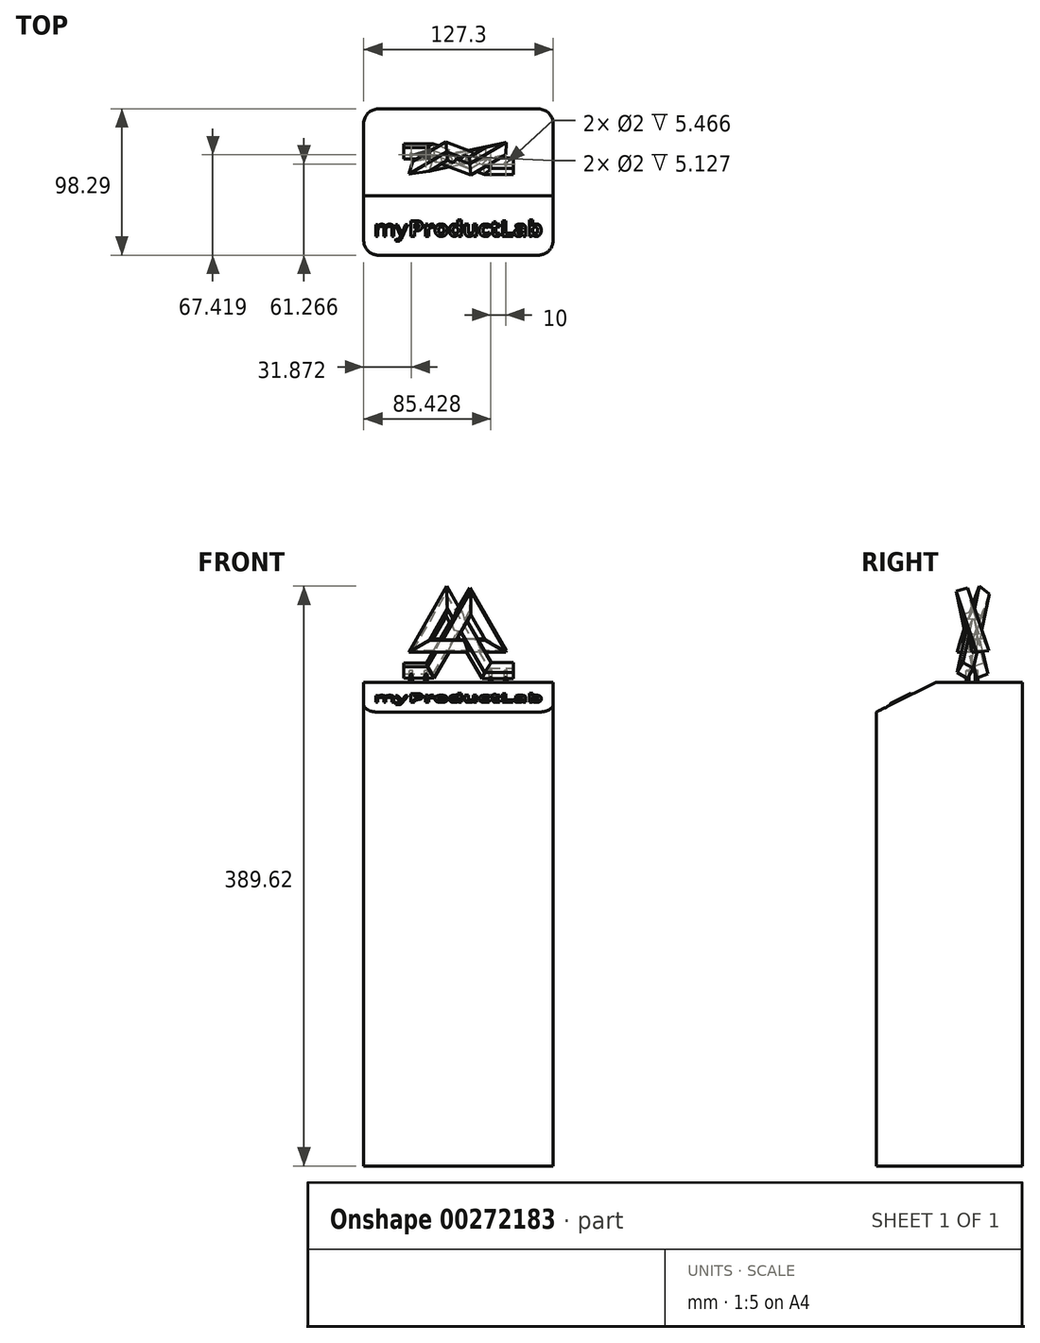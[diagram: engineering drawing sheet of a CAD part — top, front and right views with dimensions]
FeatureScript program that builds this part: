
annotation { "Feature Type Name" : "Feature", "Feature Type Description" : "" }
export const myFeature = defineFeature(function(context is Context, id is Id, definition is map)
    precondition{}
    {
        {
            var Q0;
            Q0=qCreatedBy(makeId("Front.planeOp"),FACE);
            var sketch = newSketch(context, id + "F0", { "sketchPlane" : qUnion([Q0])});
            skLineSegment(sketch, "E0", {"start": v(-36.78, 0) * mm, "end": v(-18.91, 0) * mm});
            skLineSegment(sketch, "E1", {"start": v(-18.91, 0) * mm, "end": v(7.93, 46.5) * mm});
            skLineSegment(sketch, "E2", {"start": v(7.93, 46.5) * mm, "end": v(25.1, 16.76) * mm});
            skLineSegment(sketch, "E3", {"start": v(25.1, 16.76) * mm, "end": v(-25.1, 16.76) * mm});
            skLineSegment(sketch, "E4", {"start": v(-25.1, 16.76) * mm, "end": v(-7.93, 46.5) * mm});
            skLineSegment(sketch, "E5", {"start": v(-7.93, 46.5) * mm, "end": v(18.91, 0) * mm});
            skLineSegment(sketch, "E6", {"start": v(18.91, 0) * mm, "end": v(36.78, 0) * mm});
            skPoint(sketch, "E7", {"position": v(0, 32.76) * mm});
            skPoint(sketch, "E8", {"position": v(0, 16.76) * mm});
            skSolve(sketch);
        }
        {
            var Q0;
            Q0=qCreatedBy(makeId("Front.planeOp"),FACE);
            cPlane(context, id + "F1", {"entities" : qUnion([Q0]), "cplaneType" : CPlaneType.OFFSET, "offset" : 10 * mm, "oppositeDirection" : true, "width" : 150 * mm, "height" : 150 * mm});
        }
        {
            var Q0;
            Q0=qCreatedBy(id+"F1.planeOp",FACE);
            var sketch = newSketch(context, id + "F2", { "sketchPlane" : qUnion([Q0])});
            skPoint(sketch, "E9", {"position": v(-36.78, 0) * mm});
            skPoint(sketch, "E10", {"position": v(-18.91, 0) * mm});
            skPoint(sketch, "E11", {"position": v(25.1, 16.76) * mm});
            skPoint(sketch, "E12", {"position": v(-7.93, 46.5) * mm});
            skSolve(sketch);
        }
        {
            var Q0;
            Q0=qCreatedBy(makeId("Front.planeOp"),FACE);
            var sketch = newSketch(context, id + "F3", { "sketchPlane" : qUnion([Q0])});
            skPoint(sketch, "E13", {"position": v(-25.1, 16.76) * mm});
            skPoint(sketch, "E14", {"position": v(7.93, 46.5) * mm});
            skPoint(sketch, "E15", {"position": v(18.91, 0) * mm});
            skPoint(sketch, "E16", {"position": v(36.78, 0) * mm});
            skSolve(sketch);
        }
        {
            var Q0;
            Q0=sQuery(id+"F2.wireOp",VERTEX,"E12");
            var Q1;
            Q1=sQuery(id+"F2.wireOp",VERTEX,"E10");
            var Q2;
            Q2=sQuery(id+"F3.wireOp",VERTEX,"E14");
            cPlane(context, id + "F4", {"entities" : qUnion([Q0, Q1, Q2]), "cplaneType" : CPlaneType.THREE_POINT, "offset" : 25 * mm, "width" : 150 * mm, "height" : 150 * mm});
        }
        {
            var Q0;
            Q0=sQuery(id+"F3.wireOp",VERTEX,"E14");
            var Q1;
            Q1=sQuery(id+"F2.wireOp",VERTEX,"E11");
            var Q2;
            Q2=sQuery(id+"F3.wireOp",VERTEX,"E13");
            cPlane(context, id + "F5", {"entities" : qUnion([Q0, Q1, Q2]), "cplaneType" : CPlaneType.THREE_POINT, "offset" : 25 * mm, "width" : 150 * mm, "height" : 150 * mm});
        }
        {
            var Q0;
            Q0=qCreatedBy(id+"F1.planeOp",FACE);
            var sketch = newSketch(context, id + "F6", { "sketchPlane" : qUnion([Q0])});
            skLineSegment(sketch, "E17", {"start": v(-36.78, 0) * mm, "end": v(-18.91, 0) * mm});
            skSolve(sketch);
        }
        {
            var Q0;
            Q0=qCreatedBy(id+"F4.planeOp",FACE);
            var sketch = newSketch(context, id + "F7", { "sketchPlane" : qUnion([Q0])});
            skLineSegment(sketch, "E18", {"start": v(21.28, 1.47) * mm, "end": v(-10.35, 46) * mm});
            skSolve(sketch);
        }
        {
            var Q0;
            Q0=qCreatedBy(id+"F5.planeOp",FACE);
            var sketch = newSketch(context, id + "F8", { "sketchPlane" : qUnion([Q0])});
            skLineSegment(sketch, "E19", {"start": v(9.7, 45.4) * mm, "end": v(27.2, 14.2) * mm});
            skSolve(sketch);
        }
        {
            var Q0;
            Q0=qCreatedBy(id+"F5.planeOp",FACE);
            var sketch = newSketch(context, id + "F9", { "sketchPlane" : qUnion([Q0])});
            skLineSegment(sketch, "E20", {"start": v(1.62, 15.29) * mm, "end": v(-23.95, 16.37) * mm});
            skLineSegment(sketch, "E21", {"start": v(27.2, 14.2) * mm, "end": v(1.62, 15.29) * mm});
            skSolve(sketch);
        }
        {
            var Q0;
            Q0=sQuery(id+"F2.wireOp",VERTEX,"E12");
            var Q1;
            Q1=sQuery(id+"F3.wireOp",VERTEX,"E13");
            var Q2;
            Q2=sQuery(id+"F2.wireOp",VERTEX,"E10");
            cPlane(context, id + "F10", {"entities" : qUnion([Q0, Q1, Q2]), "cplaneType" : CPlaneType.THREE_POINT, "offset" : 25 * mm, "width" : 150 * mm, "height" : 150 * mm});
        }
        {
            var Q0;
            Q0=qCreatedBy(id+"F10.planeOp",FACE);
            var sketch = newSketch(context, id + "F11", { "sketchPlane" : qUnion([Q0])});
            skLineSegment(sketch, "E22", {"start": v(-8.31, 43.03) * mm, "end": v(15.48, 16.33) * mm});
            skSolve(sketch);
        }
        {
            var Q0;
            Q0=sQuery(id+"F2.wireOp",VERTEX,"E12");
            var Q1;
            Q1=sQuery(id+"F3.wireOp",VERTEX,"E15");
            var Q2;
            Q2=sQuery(id+"F3.wireOp",VERTEX,"E16");
            cPlane(context, id + "F12", {"entities" : qUnion([Q0, Q1, Q2]), "cplaneType" : CPlaneType.THREE_POINT, "offset" : 25 * mm, "width" : 150 * mm, "height" : 150 * mm});
        }
        {
            var Q0;
            Q0=qCreatedBy(id+"F12.planeOp",FACE);
            var sketch = newSketch(context, id + "F13", { "sketchPlane" : qUnion([Q0])});
            skLineSegment(sketch, "E23", {"start": v(7.93, 47.56) * mm, "end": v(-18.91, 0) * mm});
            skLineSegment(sketch, "E24", {"start": v(-18.91, 0) * mm, "end": v(-36.78, 0) * mm});
            skSolve(sketch);
        }
        {
            var Q0;
            Q0=sQuery(id+"F6.wireOp",EDGE,"E17");
            var Q1;
            Q1=sQuery(id+"F6.wireOp",VERTEX,"E17.start");
            cPlane(context, id + "F14", {"entities" : qUnion([Q0, Q1]), "cplaneType" : CPlaneType.LINE_POINT, "offset" : 25 * mm, "width" : 150 * mm, "height" : 150 * mm});
        }
        {
            var Q0;
            Q0=qCreatedBy(id+"F14.planeOp",FACE);
            var sketch = newSketch(context, id + "F15", { "sketchPlane" : qUnion([Q0])});
            skLineSegment(sketch, "E25.bottom", {"start": v(6, 4) * mm, "end": v(14, 4) * mm, "construction": true});
            skLineSegment(sketch, "E25.top", {"start": v(6, -4) * mm, "end": v(14, -4) * mm, "construction": true});
            skLineSegment(sketch, "E25.left", {"start": v(6, 4) * mm, "end": v(6, -4) * mm, "construction": true});
            skLineSegment(sketch, "E25.right", {"start": v(14, 4) * mm, "end": v(14, -4) * mm, "construction": true});
            skPoint(sketch, "E25.middle", {"position": v(10, 0) * mm});
            skLineSegment(sketch, "E26", {"start": v(7.6, -5.13) * mm, "end": v(15.13, -2.4) * mm});
            skLineSegment(sketch, "E27", {"start": v(15.13, -2.4) * mm, "end": v(12.4, 5.13) * mm});
            skLineSegment(sketch, "E28", {"start": v(12.4, 5.13) * mm, "end": v(4.87, 2.4) * mm});
            skLineSegment(sketch, "E29", {"start": v(4.87, 2.4) * mm, "end": v(7.6, -5.13) * mm});
            skLineSegment(sketch, "E30", {"start": v(7.6, -5.13) * mm, "end": v(12.4, 5.13) * mm, "construction": true});
            skLineSegment(sketch, "E31", {"start": v(15.13, -2.4) * mm, "end": v(4.87, 2.4) * mm, "construction": true});
            skSolve(sketch);
        }
        {
            var Q0;
            Q0=makeQuery(id+"F15.imprint","IMPRINT",FACE,{"disambiguationData":[TD([[makeQuery(id+"F15.imprint","IMPRINT",EDGE,{"derivedFrom":sQuery(id+"F15.wireOp",EDGE,"E26")}),1.0]])]});
            var Q1;
            Q1=sQuery(id+"F6.wireOp",EDGE,"E17");
            var Q2;
            Q2=sQuery(id+"F7.wireOp",EDGE,"E18");
            var Q3;
            Q3=sQuery(id+"F8.wireOp",EDGE,"E19");
            var Q4;
            Q4=sQuery(id+"F9.wireOp",EDGE,"E21");
            sweep(context, id + "F16", {"profiles" : qUnion([Q0]), "path" : qUnion([Q1, Q2, Q3, Q4])});
        }
        {
            var Q0;
            Q0=sQuery(id+"F13.wireOp",EDGE,"E24");
            var Q1;
            Q1=sQuery(id+"F13.wireOp",VERTEX,"E24.end");
            cPlane(context, id + "F17", {"entities" : qUnion([Q0, Q1]), "cplaneType" : CPlaneType.LINE_POINT, "offset" : 25 * mm, "width" : 150 * mm, "height" : 150 * mm});
        }
        {
            var Q0;
            Q0=qCreatedBy(id+"F17.planeOp",FACE);
            var sketch = newSketch(context, id + "F18", { "sketchPlane" : qUnion([Q0])});
            skLineSegment(sketch, "E32.bottom", {"start": v(4, -4) * mm, "end": v(-4, -4) * mm});
            skLineSegment(sketch, "E32.top", {"start": v(4, 4) * mm, "end": v(-4, 4) * mm});
            skLineSegment(sketch, "E32.left", {"start": v(4, -4) * mm, "end": v(4, 4) * mm});
            skLineSegment(sketch, "E32.right", {"start": v(-4, -4) * mm, "end": v(-4, 4) * mm});
            skPoint(sketch, "E32.middle", {"position": v(0, 0) * mm});
            skSolve(sketch);
        }
        {
            var Q0;
            Q0=makeQuery(id+"F16.opSweep","CAP_FACE",FACE,{"disambiguationData":[OSD([sQuery(id+"F9.wireOp",VERTEX,"E21.end"),sQuery(id+"F15.wireOp",EDGE,"E26"),sQuery(id+"F15.wireOp",EDGE,"E27"),sQuery(id+"F15.wireOp",EDGE,"E28"),sQuery(id+"F15.wireOp",EDGE,"E29")])],"isStart":false});
            var sketch = newSketch(context, id + "F19", { "sketchPlane" : qUnion([Q0])});
            skLineSegment(sketch, "E33.0", {"start": v(-9.24, 13.13) * mm, "end": v(-1.27, 12.43) * mm});
            skLineSegment(sketch, "E34", {"start": v(-1.27, 12.43) * mm, "end": v(-0.57, 20.4) * mm});
            skLineSegment(sketch, "E35", {"start": v(-0.57, 20.4) * mm, "end": v(-8.54, 21.1) * mm});
            skLineSegment(sketch, "E36", {"start": v(-8.54, 21.1) * mm, "end": v(-9.24, 13.13) * mm});
            skSolve(sketch);
        }
        {
            var Q0;
            Q0 = qSketchRegion(id + "F19", true);
            var Q1;
            Q1=sQuery(id+"F9.wireOp",EDGE,"E20");
            var Q2;
            Q2=sQuery(id+"F11.wireOp",EDGE,"E22");
            var Q3;
            Q3=sQuery(id+"F13.wireOp",EDGE,"E23");
            var Q4;
            Q4=sQuery(id+"F13.wireOp",EDGE,"E24");
            sweep(context, id + "F20", {"operationType" : NewBodyOperationType.ADD, "profiles" : qUnion([Q0]), "path" : qUnion([Q1, Q2, Q3, Q4])});
        }
        {
            var Q0;
            Q0=qCreatedBy(makeId("Top.planeOp"),FACE);
            var sketch = newSketch(context, id + "F21", { "sketchPlane" : qUnion([Q0])});
            skCircle(sketch, "E37", {"center": v(-31.78, 7.6) * mm, "radius": 1 * mm});
            skCircle(sketch, "E38", {"center": v(-21.78, 7.6) * mm, "radius": 1 * mm});
            skCircle(sketch, "E39", {"center": v(21.78, 1.46) * mm, "radius": 1 * mm});
            skCircle(sketch, "E40", {"center": v(31.78, 1.46) * mm, "radius": 1 * mm});
            skSolve(sketch);
        }
        {
            var Q0;
            Q0 = qSketchRegion(id + "F21", true);
            extrude(context, id + "F22", {"entities" : qUnion([Q0]), "operationType" : NewBodyOperationType.REMOVE, "oppositeDirection" : true, "depth" : 25 * mm});
        }
        {
            var Q0;
            Q0 = qSketchRegion(id + "F21", true);
            extrude(context, id + "F23", {"entities" : qUnion([Q0]), "oppositeDirection" : true, "depth" : 10 * mm});
        }
        {
            var Q0;
            Q0=qCreatedBy(makeId("Top.planeOp"),FACE);
            cPlane(context, id + "F24", {"entities" : qUnion([Q0]), "cplaneType" : CPlaneType.OFFSET, "offset" : 8 * mm, "oppositeDirection" : true, "width" : 150 * mm, "height" : 150 * mm});
        }
        {
            var Q0;
            Q0=qCreatedBy(id+"F24.planeOp",FACE);
            var sketch = newSketch(context, id + "F25", { "sketchPlane" : qUnion([Q0])});
            skLineSegment(sketch, "E41.bottom", {"start": v(-63.65, 38.48) * mm, "end": v(63.65, 38.48) * mm});
            skLineSegment(sketch, "E41.top", {"start": v(-63.65, -59.81) * mm, "end": v(63.65, -59.81) * mm});
            skLineSegment(sketch, "E41.left", {"start": v(-63.65, 38.48) * mm, "end": v(-63.65, -59.81) * mm});
            skLineSegment(sketch, "E41.right", {"start": v(63.65, 38.48) * mm, "end": v(63.65, -59.81) * mm});
            skPoint(sketch, "E41.middle", {"position": v(0, -10.67) * mm});
            skSolve(sketch);
        }
        {
            var Q0;
            Q0 = qSketchRegion(id + "F25", true);
            extrude(context, id + "F26", {"entities" : qUnion([Q0]), "oppositeDirection" : true, "depth" : 25 * mm});
        }
        {
            var Q0;
            Q0=makeQuery(id+"F26.opExtrude","CAP_EDGE",EDGE,{"disambiguationData":[OSD([sQuery(id+"F25.wireOp",EDGE,"E41.top")])],"isStart":true});
            chamfer(context, id + "F27", {"entities" : qUnion([Q0]), "chamferType" : ChamferType.TWO_OFFSETS, "width1" : 40 * mm, "oppositeDirection" : false, "width2" : 20 * mm, "tangentPropagation" : true});
        }
        {
            var Q0;
            Q0=makeQuery(id+"F27.opChamfer","BLEND_FACE",FACE,{"disambiguationData":[OSD([sQuery(id+"F25.wireOp",EDGE,"E41.top")])]});
            var sketch = newSketch(context, id + "F28", { "sketchPlane" : qUnion([Q0])});
            skText(sketch, "E42", { "text": "ProductLab", "fontName": "OpenSans-Bold.ttf"});
            skText(sketch, "E43", { "text": "my", "fontName": "OpenSans-Regular.ttf"});
            const initialGuessF28  = {"E42": [-0.03325, -0.05127, 1, 0, 0.01123], "E43": [-0.05665, -0.05127, 1, 0, 0.01125]};
            skSetInitialGuess(sketch, initialGuessF28);
            skSolve(sketch);
        }
        {
            var Q0;
            Q0 = qSketchRegion(id + "F28", true);
            extrude(context, id + "F29", {"entities" : qUnion([Q0]), "depth" : 1 * mm, "hasSecondDirection" : true, "secondDirectionOppositeDirection" : true, "secondDirectionDepth" : 1 * mm});
        }
        {
            var Q0;
            Q0=makeQuery(id+"F29.opExtrude","SWEPT_BODY",BODY,{"disambiguationData":[OSD([sQuery(id+"F28.wireOp",EDGE,"E43.sketch_text.stroke-0"),sQuery(id+"F28.wireOp",EDGE,"E43.sketch_text.stroke-1"),sQuery(id+"F28.wireOp",EDGE,"E43.sketch_text.stroke-2"),sQuery(id+"F28.wireOp",EDGE,"E43.sketch_text.stroke-3"),sQuery(id+"F28.wireOp",EDGE,"E43.sketch_text.stroke-4"),sQuery(id+"F28.wireOp",EDGE,"E43.sketch_text.stroke-5"),sQuery(id+"F28.wireOp",EDGE,"E43.sketch_text.stroke-6"),sQuery(id+"F28.wireOp",EDGE,"E43.sketch_text.stroke-7"),sQuery(id+"F28.wireOp",EDGE,"E43.sketch_text.stroke-8"),sQuery(id+"F28.wireOp",EDGE,"E43.sketch_text.stroke-9"),sQuery(id+"F28.wireOp",EDGE,"E43.sketch_text.stroke-10"),sQuery(id+"F28.wireOp",EDGE,"E43.sketch_text.stroke-11"),sQuery(id+"F28.wireOp",EDGE,"E43.sketch_text.stroke-12"),sQuery(id+"F28.wireOp",EDGE,"E43.sketch_text.stroke-13"),sQuery(id+"F28.wireOp",EDGE,"E43.sketch_text.stroke-14"),sQuery(id+"F28.wireOp",EDGE,"E43.sketch_text.stroke-15"),sQuery(id+"F28.wireOp",EDGE,"E43.sketch_text.stroke-16"),sQuery(id+"F28.wireOp",EDGE,"E43.sketch_text.stroke-17"),sQuery(id+"F28.wireOp",EDGE,"E43.sketch_text.stroke-18"),sQuery(id+"F28.wireOp",EDGE,"E43.sketch_text.stroke-19"),sQuery(id+"F28.wireOp",EDGE,"E43.sketch_text.stroke-20"),sQuery(id+"F28.wireOp",EDGE,"E43.sketch_text.stroke-21"),sQuery(id+"F28.wireOp",EDGE,"E43.sketch_text.stroke-22"),sQuery(id+"F28.wireOp",EDGE,"E43.sketch_text.stroke-23"),sQuery(id+"F28.wireOp",EDGE,"E43.sketch_text.stroke-24"),sQuery(id+"F28.wireOp",EDGE,"E43.sketch_text.stroke-25"),sQuery(id+"F28.wireOp",EDGE,"E43.sketch_text.stroke-26"),sQuery(id+"F28.wireOp",EDGE,"E43.sketch_text.stroke-27")])]});
            var Q1;
            Q1=makeQuery(id+"F29.opExtrude","SWEPT_BODY",BODY,{"disambiguationData":[OSD([sQuery(id+"F28.wireOp",EDGE,"E43.sketch_text.stroke-28"),sQuery(id+"F28.wireOp",EDGE,"E43.sketch_text.stroke-29"),sQuery(id+"F28.wireOp",EDGE,"E43.sketch_text.stroke-30"),sQuery(id+"F28.wireOp",EDGE,"E43.sketch_text.stroke-31"),sQuery(id+"F28.wireOp",EDGE,"E43.sketch_text.stroke-32"),sQuery(id+"F28.wireOp",EDGE,"E43.sketch_text.stroke-33"),sQuery(id+"F28.wireOp",EDGE,"E43.sketch_text.stroke-34"),sQuery(id+"F28.wireOp",EDGE,"E43.sketch_text.stroke-35"),sQuery(id+"F28.wireOp",EDGE,"E43.sketch_text.stroke-36"),sQuery(id+"F28.wireOp",EDGE,"E43.sketch_text.stroke-37"),sQuery(id+"F28.wireOp",EDGE,"E43.sketch_text.stroke-38"),sQuery(id+"F28.wireOp",EDGE,"E43.sketch_text.stroke-39"),sQuery(id+"F28.wireOp",EDGE,"E43.sketch_text.stroke-40"),sQuery(id+"F28.wireOp",EDGE,"E43.sketch_text.stroke-41"),sQuery(id+"F28.wireOp",EDGE,"E43.sketch_text.stroke-42"),sQuery(id+"F28.wireOp",EDGE,"E43.sketch_text.stroke-43")])]});
            var Q2;
            Q2=makeQuery(id+"F29.opExtrude","SWEPT_BODY",BODY,{"disambiguationData":[OSD([sQuery(id+"F28.wireOp",EDGE,"E42.sketch_text.stroke-0"),sQuery(id+"F28.wireOp",EDGE,"E42.sketch_text.stroke-1"),sQuery(id+"F28.wireOp",EDGE,"E42.sketch_text.stroke-2"),sQuery(id+"F28.wireOp",EDGE,"E42.sketch_text.stroke-3"),sQuery(id+"F28.wireOp",EDGE,"E42.sketch_text.stroke-4"),sQuery(id+"F28.wireOp",EDGE,"E42.sketch_text.stroke-5"),sQuery(id+"F28.wireOp",EDGE,"E42.sketch_text.stroke-6"),sQuery(id+"F28.wireOp",EDGE,"E42.sketch_text.stroke-7"),sQuery(id+"F28.wireOp",EDGE,"E42.sketch_text.stroke-8"),sQuery(id+"F28.wireOp",EDGE,"E42.sketch_text.stroke-9"),sQuery(id+"F28.wireOp",EDGE,"E42.sketch_text.stroke-10"),sQuery(id+"F28.wireOp",EDGE,"E42.sketch_text.stroke-11"),sQuery(id+"F28.wireOp",EDGE,"E42.sketch_text.stroke-12"),sQuery(id+"F28.wireOp",EDGE,"E42.sketch_text.stroke-13"),sQuery(id+"F28.wireOp",EDGE,"E42.sketch_text.stroke-14"),sQuery(id+"F28.wireOp",EDGE,"E42.sketch_text.stroke-15")])]});
            var Q3;
            Q3=makeQuery(id+"F29.opExtrude","SWEPT_BODY",BODY,{"disambiguationData":[OSD([sQuery(id+"F28.wireOp",EDGE,"E42.sketch_text.stroke-16"),sQuery(id+"F28.wireOp",EDGE,"E42.sketch_text.stroke-17"),sQuery(id+"F28.wireOp",EDGE,"E42.sketch_text.stroke-18"),sQuery(id+"F28.wireOp",EDGE,"E42.sketch_text.stroke-19"),sQuery(id+"F28.wireOp",EDGE,"E42.sketch_text.stroke-20"),sQuery(id+"F28.wireOp",EDGE,"E42.sketch_text.stroke-21"),sQuery(id+"F28.wireOp",EDGE,"E42.sketch_text.stroke-22"),sQuery(id+"F28.wireOp",EDGE,"E42.sketch_text.stroke-23"),sQuery(id+"F28.wireOp",EDGE,"E42.sketch_text.stroke-24"),sQuery(id+"F28.wireOp",EDGE,"E42.sketch_text.stroke-25"),sQuery(id+"F28.wireOp",EDGE,"E42.sketch_text.stroke-26"),sQuery(id+"F28.wireOp",EDGE,"E42.sketch_text.stroke-27"),sQuery(id+"F28.wireOp",EDGE,"E42.sketch_text.stroke-28")])]});
            var Q4;
            Q4=makeQuery(id+"F29.opExtrude","SWEPT_BODY",BODY,{"disambiguationData":[OSD([sQuery(id+"F28.wireOp",EDGE,"E42.sketch_text.stroke-29"),sQuery(id+"F28.wireOp",EDGE,"E42.sketch_text.stroke-30"),sQuery(id+"F28.wireOp",EDGE,"E42.sketch_text.stroke-31"),sQuery(id+"F28.wireOp",EDGE,"E42.sketch_text.stroke-32"),sQuery(id+"F28.wireOp",EDGE,"E42.sketch_text.stroke-33"),sQuery(id+"F28.wireOp",EDGE,"E42.sketch_text.stroke-34"),sQuery(id+"F28.wireOp",EDGE,"E42.sketch_text.stroke-35"),sQuery(id+"F28.wireOp",EDGE,"E42.sketch_text.stroke-36"),sQuery(id+"F28.wireOp",EDGE,"E42.sketch_text.stroke-37"),sQuery(id+"F28.wireOp",EDGE,"E42.sketch_text.stroke-38"),sQuery(id+"F28.wireOp",EDGE,"E42.sketch_text.stroke-39"),sQuery(id+"F28.wireOp",EDGE,"E42.sketch_text.stroke-40"),sQuery(id+"F28.wireOp",EDGE,"E42.sketch_text.stroke-41"),sQuery(id+"F28.wireOp",EDGE,"E42.sketch_text.stroke-42"),sQuery(id+"F28.wireOp",EDGE,"E42.sketch_text.stroke-43"),sQuery(id+"F28.wireOp",EDGE,"E42.sketch_text.stroke-44"),sQuery(id+"F28.wireOp",EDGE,"E42.sketch_text.stroke-45"),sQuery(id+"F28.wireOp",EDGE,"E42.sketch_text.stroke-46")])]});
            var Q5;
            Q5=makeQuery(id+"F29.opExtrude","SWEPT_BODY",BODY,{"disambiguationData":[OSD([sQuery(id+"F28.wireOp",EDGE,"E42.sketch_text.stroke-47"),sQuery(id+"F28.wireOp",EDGE,"E42.sketch_text.stroke-48"),sQuery(id+"F28.wireOp",EDGE,"E42.sketch_text.stroke-49"),sQuery(id+"F28.wireOp",EDGE,"E42.sketch_text.stroke-50"),sQuery(id+"F28.wireOp",EDGE,"E42.sketch_text.stroke-51"),sQuery(id+"F28.wireOp",EDGE,"E42.sketch_text.stroke-52"),sQuery(id+"F28.wireOp",EDGE,"E42.sketch_text.stroke-53"),sQuery(id+"F28.wireOp",EDGE,"E42.sketch_text.stroke-54"),sQuery(id+"F28.wireOp",EDGE,"E42.sketch_text.stroke-55"),sQuery(id+"F28.wireOp",EDGE,"E42.sketch_text.stroke-56"),sQuery(id+"F28.wireOp",EDGE,"E42.sketch_text.stroke-57"),sQuery(id+"F28.wireOp",EDGE,"E42.sketch_text.stroke-58"),sQuery(id+"F28.wireOp",EDGE,"E42.sketch_text.stroke-59"),sQuery(id+"F28.wireOp",EDGE,"E42.sketch_text.stroke-60"),sQuery(id+"F28.wireOp",EDGE,"E42.sketch_text.stroke-61"),sQuery(id+"F28.wireOp",EDGE,"E42.sketch_text.stroke-62"),sQuery(id+"F28.wireOp",EDGE,"E42.sketch_text.stroke-63"),sQuery(id+"F28.wireOp",EDGE,"E42.sketch_text.stroke-64"),sQuery(id+"F28.wireOp",EDGE,"E42.sketch_text.stroke-65"),sQuery(id+"F28.wireOp",EDGE,"E42.sketch_text.stroke-66"),sQuery(id+"F28.wireOp",EDGE,"E42.sketch_text.stroke-67"),sQuery(id+"F28.wireOp",EDGE,"E42.sketch_text.stroke-68"),sQuery(id+"F28.wireOp",EDGE,"E42.sketch_text.stroke-69")])]});
            var Q6;
            Q6=makeQuery(id+"F29.opExtrude","SWEPT_BODY",BODY,{"disambiguationData":[OSD([sQuery(id+"F28.wireOp",EDGE,"E42.sketch_text.stroke-70"),sQuery(id+"F28.wireOp",EDGE,"E42.sketch_text.stroke-71"),sQuery(id+"F28.wireOp",EDGE,"E42.sketch_text.stroke-72"),sQuery(id+"F28.wireOp",EDGE,"E42.sketch_text.stroke-73"),sQuery(id+"F28.wireOp",EDGE,"E42.sketch_text.stroke-74"),sQuery(id+"F28.wireOp",EDGE,"E42.sketch_text.stroke-75"),sQuery(id+"F28.wireOp",EDGE,"E42.sketch_text.stroke-76"),sQuery(id+"F28.wireOp",EDGE,"E42.sketch_text.stroke-77"),sQuery(id+"F28.wireOp",EDGE,"E42.sketch_text.stroke-78"),sQuery(id+"F28.wireOp",EDGE,"E42.sketch_text.stroke-79"),sQuery(id+"F28.wireOp",EDGE,"E42.sketch_text.stroke-80"),sQuery(id+"F28.wireOp",EDGE,"E42.sketch_text.stroke-81"),sQuery(id+"F28.wireOp",EDGE,"E42.sketch_text.stroke-82"),sQuery(id+"F28.wireOp",EDGE,"E42.sketch_text.stroke-83"),sQuery(id+"F28.wireOp",EDGE,"E42.sketch_text.stroke-84"),sQuery(id+"F28.wireOp",EDGE,"E42.sketch_text.stroke-85"),sQuery(id+"F28.wireOp",EDGE,"E42.sketch_text.stroke-86")])]});
            var Q7;
            Q7=makeQuery(id+"F29.opExtrude","SWEPT_BODY",BODY,{"disambiguationData":[OSD([sQuery(id+"F28.wireOp",EDGE,"E42.sketch_text.stroke-87"),sQuery(id+"F28.wireOp",EDGE,"E42.sketch_text.stroke-88"),sQuery(id+"F28.wireOp",EDGE,"E42.sketch_text.stroke-89"),sQuery(id+"F28.wireOp",EDGE,"E42.sketch_text.stroke-90"),sQuery(id+"F28.wireOp",EDGE,"E42.sketch_text.stroke-91"),sQuery(id+"F28.wireOp",EDGE,"E42.sketch_text.stroke-92"),sQuery(id+"F28.wireOp",EDGE,"E42.sketch_text.stroke-93"),sQuery(id+"F28.wireOp",EDGE,"E42.sketch_text.stroke-94"),sQuery(id+"F28.wireOp",EDGE,"E42.sketch_text.stroke-95"),sQuery(id+"F28.wireOp",EDGE,"E42.sketch_text.stroke-96"),sQuery(id+"F28.wireOp",EDGE,"E42.sketch_text.stroke-97"),sQuery(id+"F28.wireOp",EDGE,"E42.sketch_text.stroke-98"),sQuery(id+"F28.wireOp",EDGE,"E42.sketch_text.stroke-99"),sQuery(id+"F28.wireOp",EDGE,"E42.sketch_text.stroke-100")])]});
            var Q8;
            Q8=makeQuery(id+"F29.opExtrude","SWEPT_BODY",BODY,{"disambiguationData":[OSD([sQuery(id+"F28.wireOp",EDGE,"E42.sketch_text.stroke-101"),sQuery(id+"F28.wireOp",EDGE,"E42.sketch_text.stroke-102"),sQuery(id+"F28.wireOp",EDGE,"E42.sketch_text.stroke-103"),sQuery(id+"F28.wireOp",EDGE,"E42.sketch_text.stroke-104"),sQuery(id+"F28.wireOp",EDGE,"E42.sketch_text.stroke-105"),sQuery(id+"F28.wireOp",EDGE,"E42.sketch_text.stroke-106"),sQuery(id+"F28.wireOp",EDGE,"E42.sketch_text.stroke-107"),sQuery(id+"F28.wireOp",EDGE,"E42.sketch_text.stroke-108"),sQuery(id+"F28.wireOp",EDGE,"E42.sketch_text.stroke-109"),sQuery(id+"F28.wireOp",EDGE,"E42.sketch_text.stroke-110"),sQuery(id+"F28.wireOp",EDGE,"E42.sketch_text.stroke-111"),sQuery(id+"F28.wireOp",EDGE,"E42.sketch_text.stroke-112"),sQuery(id+"F28.wireOp",EDGE,"E42.sketch_text.stroke-113"),sQuery(id+"F28.wireOp",EDGE,"E42.sketch_text.stroke-114"),sQuery(id+"F28.wireOp",EDGE,"E42.sketch_text.stroke-115"),sQuery(id+"F28.wireOp",EDGE,"E42.sketch_text.stroke-116"),sQuery(id+"F28.wireOp",EDGE,"E42.sketch_text.stroke-117"),sQuery(id+"F28.wireOp",EDGE,"E42.sketch_text.stroke-118")])]});
            var Q9;
            Q9=makeQuery(id+"F29.opExtrude","SWEPT_BODY",BODY,{"disambiguationData":[OSD([sQuery(id+"F28.wireOp",EDGE,"E42.sketch_text.stroke-119"),sQuery(id+"F28.wireOp",EDGE,"E42.sketch_text.stroke-120"),sQuery(id+"F28.wireOp",EDGE,"E42.sketch_text.stroke-121"),sQuery(id+"F28.wireOp",EDGE,"E42.sketch_text.stroke-122"),sQuery(id+"F28.wireOp",EDGE,"E42.sketch_text.stroke-123"),sQuery(id+"F28.wireOp",EDGE,"E42.sketch_text.stroke-124")])]});
            var Q10;
            Q10=makeQuery(id+"F29.opExtrude","SWEPT_BODY",BODY,{"disambiguationData":[OSD([sQuery(id+"F28.wireOp",EDGE,"E42.sketch_text.stroke-125"),sQuery(id+"F28.wireOp",EDGE,"E42.sketch_text.stroke-126"),sQuery(id+"F28.wireOp",EDGE,"E42.sketch_text.stroke-127"),sQuery(id+"F28.wireOp",EDGE,"E42.sketch_text.stroke-128"),sQuery(id+"F28.wireOp",EDGE,"E42.sketch_text.stroke-129"),sQuery(id+"F28.wireOp",EDGE,"E42.sketch_text.stroke-130"),sQuery(id+"F28.wireOp",EDGE,"E42.sketch_text.stroke-131"),sQuery(id+"F28.wireOp",EDGE,"E42.sketch_text.stroke-132"),sQuery(id+"F28.wireOp",EDGE,"E42.sketch_text.stroke-133"),sQuery(id+"F28.wireOp",EDGE,"E42.sketch_text.stroke-134"),sQuery(id+"F28.wireOp",EDGE,"E42.sketch_text.stroke-135"),sQuery(id+"F28.wireOp",EDGE,"E42.sketch_text.stroke-136"),sQuery(id+"F28.wireOp",EDGE,"E42.sketch_text.stroke-137"),sQuery(id+"F28.wireOp",EDGE,"E42.sketch_text.stroke-138"),sQuery(id+"F28.wireOp",EDGE,"E42.sketch_text.stroke-139"),sQuery(id+"F28.wireOp",EDGE,"E42.sketch_text.stroke-140"),sQuery(id+"F28.wireOp",EDGE,"E42.sketch_text.stroke-141"),sQuery(id+"F28.wireOp",EDGE,"E42.sketch_text.stroke-142"),sQuery(id+"F28.wireOp",EDGE,"E42.sketch_text.stroke-143"),sQuery(id+"F28.wireOp",EDGE,"E42.sketch_text.stroke-144"),sQuery(id+"F28.wireOp",EDGE,"E42.sketch_text.stroke-145"),sQuery(id+"F28.wireOp",EDGE,"E42.sketch_text.stroke-146"),sQuery(id+"F28.wireOp",EDGE,"E42.sketch_text.stroke-147"),sQuery(id+"F28.wireOp",EDGE,"E42.sketch_text.stroke-148"),sQuery(id+"F28.wireOp",EDGE,"E42.sketch_text.stroke-149")])]});
            var Q11;
            Q11=makeQuery(id+"F29.opExtrude","SWEPT_BODY",BODY,{"disambiguationData":[OSD([sQuery(id+"F28.wireOp",EDGE,"E42.sketch_text.stroke-150"),sQuery(id+"F28.wireOp",EDGE,"E42.sketch_text.stroke-151"),sQuery(id+"F28.wireOp",EDGE,"E42.sketch_text.stroke-152"),sQuery(id+"F28.wireOp",EDGE,"E42.sketch_text.stroke-153"),sQuery(id+"F28.wireOp",EDGE,"E42.sketch_text.stroke-154"),sQuery(id+"F28.wireOp",EDGE,"E42.sketch_text.stroke-155"),sQuery(id+"F28.wireOp",EDGE,"E42.sketch_text.stroke-156"),sQuery(id+"F28.wireOp",EDGE,"E42.sketch_text.stroke-157"),sQuery(id+"F28.wireOp",EDGE,"E42.sketch_text.stroke-158"),sQuery(id+"F28.wireOp",EDGE,"E42.sketch_text.stroke-159"),sQuery(id+"F28.wireOp",EDGE,"E42.sketch_text.stroke-160"),sQuery(id+"F28.wireOp",EDGE,"E42.sketch_text.stroke-161"),sQuery(id+"F28.wireOp",EDGE,"E42.sketch_text.stroke-162"),sQuery(id+"F28.wireOp",EDGE,"E42.sketch_text.stroke-163"),sQuery(id+"F28.wireOp",EDGE,"E42.sketch_text.stroke-164"),sQuery(id+"F28.wireOp",EDGE,"E42.sketch_text.stroke-165"),sQuery(id+"F28.wireOp",EDGE,"E42.sketch_text.stroke-166"),sQuery(id+"F28.wireOp",EDGE,"E42.sketch_text.stroke-167"),sQuery(id+"F28.wireOp",EDGE,"E42.sketch_text.stroke-168"),sQuery(id+"F28.wireOp",EDGE,"E42.sketch_text.stroke-169"),sQuery(id+"F28.wireOp",EDGE,"E42.sketch_text.stroke-170"),sQuery(id+"F28.wireOp",EDGE,"E42.sketch_text.stroke-171"),sQuery(id+"F28.wireOp",EDGE,"E42.sketch_text.stroke-172")])]});
            var Q12;
            Q12=makeQuery(id+"F26.opExtrude","SWEPT_BODY",BODY,{"disambiguationData":[OSD([sQuery(id+"F25.wireOp",EDGE,"E41.bottom"),sQuery(id+"F25.wireOp",EDGE,"E41.top"),sQuery(id+"F25.wireOp",EDGE,"E41.left"),sQuery(id+"F25.wireOp",EDGE,"E41.right")])]});
            booleanBodies(context, id + "F30", {"operationType" : BooleanOperationType.SUBTRACTION, "tools" : qUnion([Q0, Q1, Q2, Q3, Q4, Q5, Q6, Q7, Q8, Q9, Q10, Q11]), "targets" : qUnion([Q12]), "keepTools" : true});
        }
        {
            var Q0;
            Q0=makeQuery(id+"F29.opExtrude","CAP_FACE",FACE,{"disambiguationData":[OSD([sQuery(id+"F28.wireOp",EDGE,"E42.sketch_text.stroke-150"),sQuery(id+"F28.wireOp",EDGE,"E42.sketch_text.stroke-151"),sQuery(id+"F28.wireOp",EDGE,"E42.sketch_text.stroke-152"),sQuery(id+"F28.wireOp",EDGE,"E42.sketch_text.stroke-153"),sQuery(id+"F28.wireOp",EDGE,"E42.sketch_text.stroke-154"),sQuery(id+"F28.wireOp",EDGE,"E42.sketch_text.stroke-155"),sQuery(id+"F28.wireOp",EDGE,"E42.sketch_text.stroke-156"),sQuery(id+"F28.wireOp",EDGE,"E42.sketch_text.stroke-157"),sQuery(id+"F28.wireOp",EDGE,"E42.sketch_text.stroke-158"),sQuery(id+"F28.wireOp",EDGE,"E42.sketch_text.stroke-159"),sQuery(id+"F28.wireOp",EDGE,"E42.sketch_text.stroke-160"),sQuery(id+"F28.wireOp",EDGE,"E42.sketch_text.stroke-161"),sQuery(id+"F28.wireOp",EDGE,"E42.sketch_text.stroke-162"),sQuery(id+"F28.wireOp",EDGE,"E42.sketch_text.stroke-163"),sQuery(id+"F28.wireOp",EDGE,"E42.sketch_text.stroke-164"),sQuery(id+"F28.wireOp",EDGE,"E42.sketch_text.stroke-165"),sQuery(id+"F28.wireOp",EDGE,"E42.sketch_text.stroke-166"),sQuery(id+"F28.wireOp",EDGE,"E42.sketch_text.stroke-167"),sQuery(id+"F28.wireOp",EDGE,"E42.sketch_text.stroke-168"),sQuery(id+"F28.wireOp",EDGE,"E42.sketch_text.stroke-169"),sQuery(id+"F28.wireOp",EDGE,"E42.sketch_text.stroke-170"),sQuery(id+"F28.wireOp",EDGE,"E42.sketch_text.stroke-171"),sQuery(id+"F28.wireOp",EDGE,"E42.sketch_text.stroke-172")])],"isStart":true});
            var sketch = newSketch(context, id + "F31", { "sketchPlane" : qUnion([Q0])});
            skLineSegment(sketch, "E44.bottom", {"start": v(55.64, 47) * mm, "end": v(-55.47, 47) * mm});
            skLineSegment(sketch, "E44.top", {"start": v(55.64, 50.26) * mm, "end": v(-55.47, 50.26) * mm});
            skLineSegment(sketch, "E44.left", {"start": v(55.64, 47) * mm, "end": v(55.64, 50.26) * mm});
            skLineSegment(sketch, "E44.right", {"start": v(-55.47, 47) * mm, "end": v(-55.47, 50.26) * mm});
            skSolve(sketch);
        }
        {
            var Q0;
            Q0 = qSketchRegion(id + "F31", true);
            extrude(context, id + "F32", {"entities" : qUnion([Q0]), "operationType" : NewBodyOperationType.ADD, "depth" : 0.1 * mm});
        }
        {
            var Q0;
            Q0=makeQuery(id+"F23.opExtrude","CAP_FACE",FACE,{"disambiguationData":[OSD([sQuery(id+"F21.wireOp",EDGE,"E40")])],"isStart":false});
            var sketch = newSketch(context, id + "F33", { "sketchPlane" : qUnion([Q0])});
            skLineSegment(sketch, "E45.bottom", {"start": v(32.73, -1.14) * mm, "end": v(-32.42, -1.14) * mm});
            skLineSegment(sketch, "E45.top", {"start": v(32.73, -8.16) * mm, "end": v(-32.42, -8.16) * mm});
            skLineSegment(sketch, "E45.left", {"start": v(32.73, -1.14) * mm, "end": v(32.73, -8.16) * mm});
            skLineSegment(sketch, "E45.right", {"start": v(-32.42, -1.14) * mm, "end": v(-32.42, -8.16) * mm});
            skSolve(sketch);
        }
        {
            var Q0;
            Q0 = qSketchRegion(id + "F33", true);
            extrude(context, id + "F34", {"entities" : qUnion([Q0]), "operationType" : NewBodyOperationType.ADD, "depth" : 0.1 * mm});
        }
        {
            var Q0;
            Q0=makeQuery(id+"F26.opExtrude","CAP_FACE",FACE,{"disambiguationData":[OSD([sQuery(id+"F25.wireOp",EDGE,"E41.bottom"),sQuery(id+"F25.wireOp",EDGE,"E41.top"),sQuery(id+"F25.wireOp",EDGE,"E41.left"),sQuery(id+"F25.wireOp",EDGE,"E41.right")])],"isStart":false});
            var sketch = newSketch(context, id + "F35", { "sketchPlane" : qUnion([Q0])});
            skLineSegment(sketch, "E46.bottom", {"start": v(83.65, 79.81) * mm, "end": v(-83.65, 79.81) * mm});
            skLineSegment(sketch, "E46.top", {"start": v(83.65, -79.81) * mm, "end": v(-83.65, -79.81) * mm});
            skLineSegment(sketch, "E46.left", {"start": v(83.65, 79.81) * mm, "end": v(83.65, -79.81) * mm});
            skLineSegment(sketch, "E46.right", {"start": v(-83.65, 79.81) * mm, "end": v(-83.65, -79.81) * mm});
            skPoint(sketch, "E46.middle", {"position": v(0, 0) * mm});
            skSolve(sketch);
        }
        {
            var Q0;
            Q0=makeQuery(id+"F26.opExtrude","SWEPT_EDGE",EDGE,{"disambiguationData":[OSD([sQuery(id+"F25.wireOp",EDGE,"E41.bottom"),sQuery(id+"F25.wireOp",EDGE,"E41.left")])]});
            var Q1;
            Q1=makeQuery(id+"F26.opExtrude","SWEPT_EDGE",EDGE,{"disambiguationData":[OSD([sQuery(id+"F25.wireOp",EDGE,"E41.bottom"),sQuery(id+"F25.wireOp",EDGE,"E41.right")])]});
            var Q2;
            Q2=makeQuery(id+"F26.opExtrude","SWEPT_EDGE",EDGE,{"disambiguationData":[OSD([sQuery(id+"F25.wireOp",EDGE,"E41.top"),sQuery(id+"F25.wireOp",EDGE,"E41.right")])]});
            var Q3;
            Q3=makeQuery(id+"F26.opExtrude","SWEPT_EDGE",EDGE,{"disambiguationData":[OSD([sQuery(id+"F25.wireOp",EDGE,"E41.top"),sQuery(id+"F25.wireOp",EDGE,"E41.left")])]});
            var Q4;
            Q4=makeQuery(id+"FYwLwIZPXlv6qP9_7.opExtrude","SWEPT_EDGE",EDGE,{"disambiguationData":[OSD([sQuery(id+"F35.wireOp",EDGE,"E46.bottom"),sQuery(id+"F35.wireOp",EDGE,"E46.left")])]});
            var Q5;
            Q5=makeQuery(id+"FYwLwIZPXlv6qP9_7.opExtrude","SWEPT_EDGE",EDGE,{"disambiguationData":[OSD([sQuery(id+"F35.wireOp",EDGE,"E46.top"),sQuery(id+"F35.wireOp",EDGE,"E46.left")])]});
            var Q6;
            Q6=makeQuery(id+"FYwLwIZPXlv6qP9_7.opExtrude","SWEPT_EDGE",EDGE,{"disambiguationData":[OSD([sQuery(id+"F35.wireOp",EDGE,"E46.bottom"),sQuery(id+"F35.wireOp",EDGE,"E46.right")])]});
            var Q7;
            Q7=makeQuery(id+"FYwLwIZPXlv6qP9_7.opExtrude","SWEPT_EDGE",EDGE,{"disambiguationData":[OSD([sQuery(id+"F35.wireOp",EDGE,"E46.top"),sQuery(id+"F35.wireOp",EDGE,"E46.right")])]});
            fillet(context, id + "F36", {"entities" : qUnion([Q0, Q1, Q2, Q3, Q4, Q5, Q6, Q7]), "radius" : 10 * mm, "tangentPropagation" : true, "allowEdgeOverflow" : false});
        }
        {
            var Q0;
            Q0=makeQuery(id+"F26.opExtrude","CAP_FACE",FACE,{"disambiguationData":[OSD([sQuery(id+"F25.wireOp",EDGE,"E41.bottom"),sQuery(id+"F25.wireOp",EDGE,"E41.top"),sQuery(id+"F25.wireOp",EDGE,"E41.left"),sQuery(id+"F25.wireOp",EDGE,"E41.right")])],"isStart":false});
            extrude(context, id + "F37", {"entities" : qUnion([Q0]), "operationType" : NewBodyOperationType.ADD, "depth" : 300 * mm});
        }
    });
